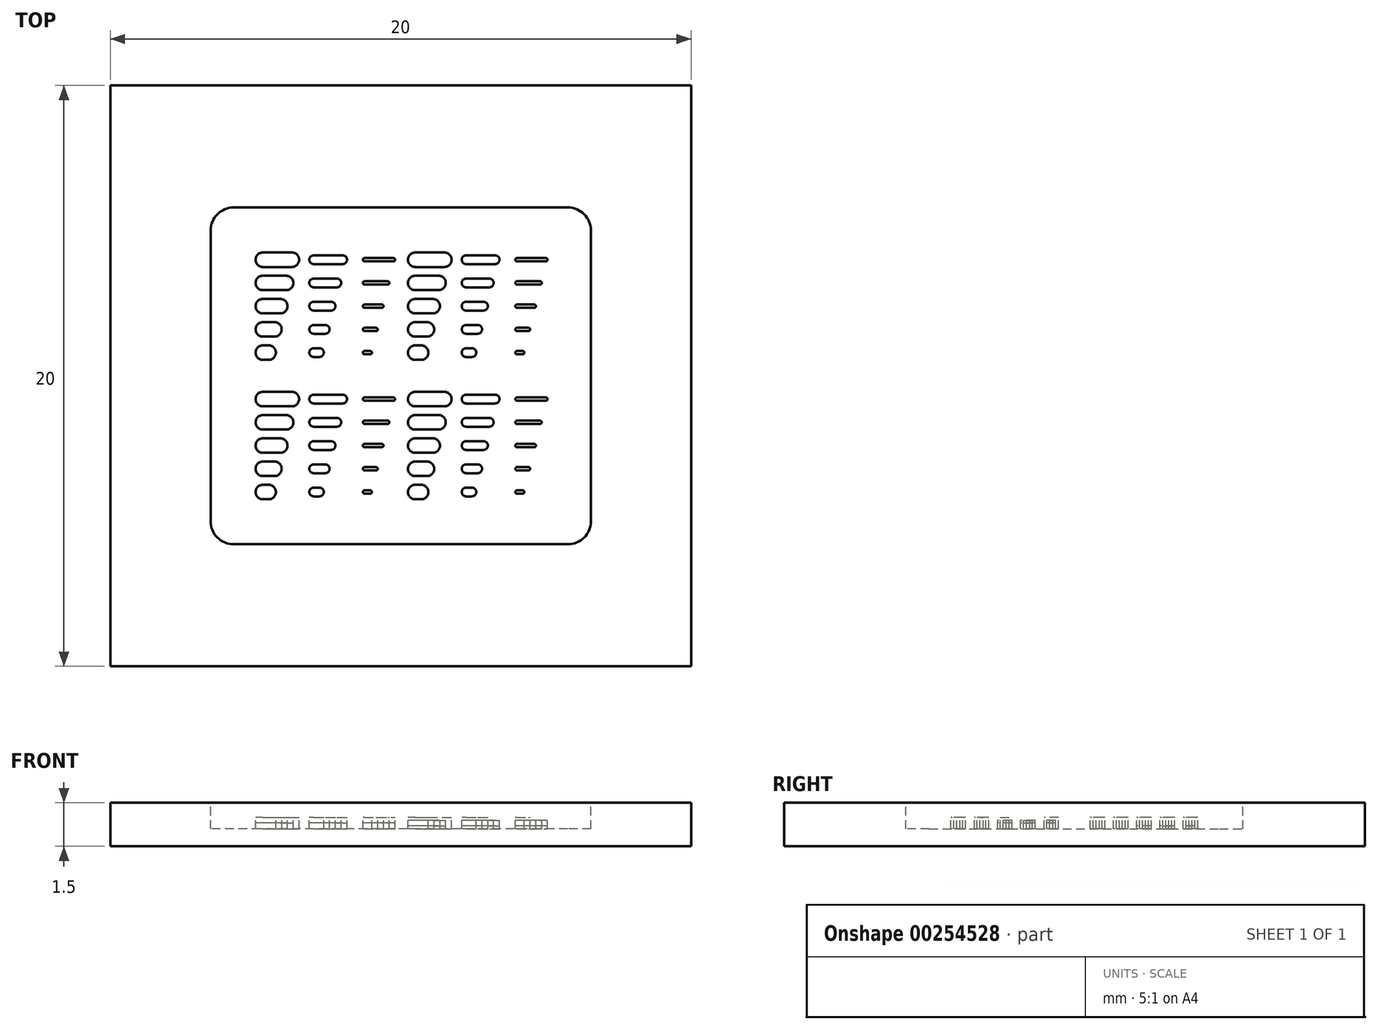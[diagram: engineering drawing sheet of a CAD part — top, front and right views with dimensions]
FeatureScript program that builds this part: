
annotation { "Feature Type Name" : "Feature", "Feature Type Description" : "" }
export const myFeature = defineFeature(function(context is Context, id is Id, definition is map)
    precondition{}
    {
        {
            var Q0;
            Q0=qCreatedBy(makeId("Top.planeOp"),FACE);
            var sketch = newSketch(context, id + "F0", { "sketchPlane" : qUnion([Q0])});
            skLineSegment(sketch, "E0.bottom", {"start": v(10, 10) * mm, "end": v(-10, 10) * mm});
            skLineSegment(sketch, "E0.top", {"start": v(10, -10) * mm, "end": v(-10, -10) * mm});
            skLineSegment(sketch, "E0.left", {"start": v(10, 10) * mm, "end": v(10, -10) * mm});
            skLineSegment(sketch, "E0.right", {"start": v(-10, 10) * mm, "end": v(-10, -10) * mm});
            skPoint(sketch, "E0.middle", {"position": v(0, 0) * mm});
            skSolve(sketch);
        }
        {
            var Q0;
            Q0=qSketchRegion(id+"F0",true);
            extrude(context, id + "F1", {"entities" : qUnion([Q0]), "oppositeDirection" : true, "depth" : 1 * mm});
        }
        {
            var Q0;
            Q0=makeQuery(id+"F1.opExtrude","CAP_FACE",FACE,{"disambiguationData":[OSD([sQuery(id+"F0.wireOp",EDGE,"E0.bottom"),sQuery(id+"F0.wireOp",EDGE,"E0.top"),sQuery(id+"F0.wireOp",EDGE,"E0.left"),sQuery(id+"F0.wireOp",EDGE,"E0.right")])],"isStart":true});
            var sketch = newSketch(context, id + "F2", { "sketchPlane" : qUnion([Q0])});
            skLineSegment(sketch, "E1.bottom", {"start": v(5.75, -5) * mm, "end": v(-5.75, -5) * mm});
            skLineSegment(sketch, "E1.top", {"start": v(5.75, 5) * mm, "end": v(-5.75, 5) * mm});
            skLineSegment(sketch, "E1.left", {"start": v(5.75, -5) * mm, "end": v(5.75, 5) * mm});
            skLineSegment(sketch, "E1.right", {"start": v(-5.75, -5) * mm, "end": v(-5.75, 5) * mm});
            skLineSegment(sketch, "E2", {"start": v(-4.75, 4) * mm, "end": v(-3.75, 4) * mm, "construction": true});
            skLineSegment(sketch, "E3", {"start": v(-4.75, 3.2) * mm, "end": v(-3.95, 3.2) * mm, "construction": true});
            skLineSegment(sketch, "E4", {"start": v(-4.75, 2.4) * mm, "end": v(-4.15, 2.4) * mm, "construction": true});
            skLineSegment(sketch, "E5", {"start": v(-4.75, 1.6) * mm, "end": v(-4.35, 1.6) * mm, "construction": true});
            skLineSegment(sketch, "E6", {"start": v(-4.75, 0.8) * mm, "end": v(-4.55, 0.8) * mm, "construction": true});
            skLineSegment(sketch, "E7.1.0.0", {"start": v(-3, 3.2) * mm, "end": v(-2.2, 3.2) * mm, "construction": true});
            skLineSegment(sketch, "E7.1.0.1", {"start": v(-3, 4) * mm, "end": v(-2, 4) * mm, "construction": true});
            skLineSegment(sketch, "E7.1.0.2", {"start": v(-3, 2.4) * mm, "end": v(-2.4, 2.4) * mm, "construction": true});
            skLineSegment(sketch, "E7.1.0.3", {"start": v(-3, 1.6) * mm, "end": v(-2.6, 1.6) * mm, "construction": true});
            skLineSegment(sketch, "E7.1.0.4", {"start": v(-3, 0.8) * mm, "end": v(-2.8, 0.8) * mm, "construction": true});
            skLineSegment(sketch, "E7.2.0.0", {"start": v(-1.25, 3.2) * mm, "end": v(-0.45, 3.2) * mm, "construction": true});
            skLineSegment(sketch, "E7.2.0.1", {"start": v(-1.25, 4) * mm, "end": v(-0.25, 4) * mm, "construction": true});
            skLineSegment(sketch, "E7.2.0.2", {"start": v(-1.25, 2.4) * mm, "end": v(-0.65, 2.4) * mm, "construction": true});
            skLineSegment(sketch, "E7.2.0.3", {"start": v(-1.25, 1.6) * mm, "end": v(-0.85, 1.6) * mm, "construction": true});
            skLineSegment(sketch, "E7.2.0.4", {"start": v(-1.25, 0.8) * mm, "end": v(-1.05, 0.8) * mm, "construction": true});
            skLineSegment(sketch, "E7.direction1", {"start": v(-4.75, 0.8) * mm, "end": v(-3, 0.8) * mm, "construction": true});
            skLineSegment(sketch, "E7.direction2", {"start": v(-4.75, 0.8) * mm, "end": v(-4.75, -4) * mm, "construction": true});
            skLineSegment(sketch, "E8.0", {"start": v(5.75, 5.8) * mm, "end": v(-5.75, 5.8) * mm});
            skLineSegment(sketch, "E8.1", {"start": v(6.55, -5) * mm, "end": v(6.55, 5) * mm});
            skLineSegment(sketch, "E8.2", {"start": v(5.75, -5.8) * mm, "end": v(-5.75, -5.8) * mm});
            skLineSegment(sketch, "E8.3", {"start": v(-6.55, -5) * mm, "end": v(-6.55, 5) * mm});
            skPoint(sketch, "E9.visualSharp", {"position": v(-6.55, 5.8) * mm});
            skArc(sketch, "E9.filletArc", {"start": v(-5.75, 5.8) * mm, "mid": v(-6.32, 5.57) * mm, "end": v(-6.55, 5) * mm});
            skPoint(sketch, "E10.visualSharp", {"position": v(6.55, 5.8) * mm});
            skArc(sketch, "E10.filletArc", {"start": v(6.55, 5) * mm, "mid": v(6.32, 5.57) * mm, "end": v(5.75, 5.8) * mm});
            skPoint(sketch, "E11.visualSharp", {"position": v(6.55, -5.8) * mm});
            skArc(sketch, "E11.filletArc", {"start": v(5.75, -5.8) * mm, "mid": v(6.32, -5.57) * mm, "end": v(6.55, -5) * mm});
            skPoint(sketch, "E12.visualSharp", {"position": v(-6.55, -5.8) * mm});
            skArc(sketch, "E12.filletArc", {"start": v(-6.55, -5) * mm, "mid": v(-6.32, -5.57) * mm, "end": v(-5.75, -5.8) * mm});
            skArc(sketch, "E13.0.startCap", {"start": v(-4.75, 0.55) * mm, "mid": v(-5, 0.8) * mm, "end": v(-4.75, 1.05) * mm});
            skArc(sketch, "E13.0.endCap", {"start": v(-4.55, 1.05) * mm, "mid": v(-4.3, 0.8) * mm, "end": v(-4.55, 0.55) * mm});
            skLineSegment(sketch, "E13.0.left", {"start": v(-4.75, 1.05) * mm, "end": v(-4.55, 1.05) * mm});
            skLineSegment(sketch, "E13.0.right", {"start": v(-4.75, 0.55) * mm, "end": v(-4.55, 0.55) * mm});
            skArc(sketch, "E13.1.startCap", {"start": v(-4.75, 1.35) * mm, "mid": v(-5, 1.6) * mm, "end": v(-4.75, 1.85) * mm});
            skArc(sketch, "E13.1.endCap", {"start": v(-4.35, 1.85) * mm, "mid": v(-4.1, 1.6) * mm, "end": v(-4.35, 1.35) * mm});
            skLineSegment(sketch, "E13.1.left", {"start": v(-4.75, 1.85) * mm, "end": v(-4.35, 1.85) * mm});
            skLineSegment(sketch, "E13.1.right", {"start": v(-4.75, 1.35) * mm, "end": v(-4.35, 1.35) * mm});
            skArc(sketch, "E13.2.startCap", {"start": v(-4.75, 2.15) * mm, "mid": v(-5, 2.4) * mm, "end": v(-4.75, 2.65) * mm});
            skArc(sketch, "E13.2.endCap", {"start": v(-4.15, 2.65) * mm, "mid": v(-3.9, 2.4) * mm, "end": v(-4.15, 2.15) * mm});
            skLineSegment(sketch, "E13.2.left", {"start": v(-4.75, 2.65) * mm, "end": v(-4.15, 2.65) * mm});
            skLineSegment(sketch, "E13.2.right", {"start": v(-4.75, 2.15) * mm, "end": v(-4.15, 2.15) * mm});
            skArc(sketch, "E13.3.startCap", {"start": v(-4.75, 2.95) * mm, "mid": v(-5, 3.2) * mm, "end": v(-4.75, 3.45) * mm});
            skArc(sketch, "E13.3.endCap", {"start": v(-3.95, 3.45) * mm, "mid": v(-3.7, 3.2) * mm, "end": v(-3.95, 2.95) * mm});
            skLineSegment(sketch, "E13.3.left", {"start": v(-4.75, 3.45) * mm, "end": v(-3.95, 3.45) * mm});
            skLineSegment(sketch, "E13.3.right", {"start": v(-4.75, 2.95) * mm, "end": v(-3.95, 2.95) * mm});
            skArc(sketch, "E13.4.startCap", {"start": v(-4.75, 3.75) * mm, "mid": v(-5, 4) * mm, "end": v(-4.75, 4.25) * mm});
            skArc(sketch, "E13.4.endCap", {"start": v(-3.75, 4.25) * mm, "mid": v(-3.5, 4) * mm, "end": v(-3.75, 3.75) * mm});
            skLineSegment(sketch, "E13.4.left", {"start": v(-4.75, 4.25) * mm, "end": v(-3.75, 4.25) * mm});
            skLineSegment(sketch, "E13.4.right", {"start": v(-4.75, 3.75) * mm, "end": v(-3.75, 3.75) * mm});
            skArc(sketch, "E14.0.startCap", {"start": v(-3, 0.65) * mm, "mid": v(-3.15, 0.8) * mm, "end": v(-3, 0.95) * mm});
            skArc(sketch, "E14.0.endCap", {"start": v(-2.8, 0.95) * mm, "mid": v(-2.65, 0.8) * mm, "end": v(-2.8, 0.65) * mm});
            skLineSegment(sketch, "E14.0.left", {"start": v(-3, 0.95) * mm, "end": v(-2.8, 0.95) * mm});
            skLineSegment(sketch, "E14.0.right", {"start": v(-3, 0.65) * mm, "end": v(-2.8, 0.65) * mm});
            skArc(sketch, "E14.1.startCap", {"start": v(-3, 1.45) * mm, "mid": v(-3.15, 1.6) * mm, "end": v(-3, 1.75) * mm});
            skArc(sketch, "E14.1.endCap", {"start": v(-2.6, 1.75) * mm, "mid": v(-2.45, 1.6) * mm, "end": v(-2.6, 1.45) * mm});
            skLineSegment(sketch, "E14.1.left", {"start": v(-3, 1.75) * mm, "end": v(-2.6, 1.75) * mm});
            skLineSegment(sketch, "E14.1.right", {"start": v(-3, 1.45) * mm, "end": v(-2.6, 1.45) * mm});
            skArc(sketch, "E14.2.startCap", {"start": v(-3, 2.25) * mm, "mid": v(-3.15, 2.4) * mm, "end": v(-3, 2.55) * mm});
            skArc(sketch, "E14.2.endCap", {"start": v(-2.4, 2.55) * mm, "mid": v(-2.25, 2.4) * mm, "end": v(-2.4, 2.25) * mm});
            skLineSegment(sketch, "E14.2.left", {"start": v(-3, 2.55) * mm, "end": v(-2.4, 2.55) * mm});
            skLineSegment(sketch, "E14.2.right", {"start": v(-3, 2.25) * mm, "end": v(-2.4, 2.25) * mm});
            skArc(sketch, "E14.3.startCap", {"start": v(-3, 3.05) * mm, "mid": v(-3.15, 3.2) * mm, "end": v(-3, 3.35) * mm});
            skArc(sketch, "E14.3.endCap", {"start": v(-2.2, 3.35) * mm, "mid": v(-2.05, 3.2) * mm, "end": v(-2.2, 3.05) * mm});
            skLineSegment(sketch, "E14.3.left", {"start": v(-3, 3.35) * mm, "end": v(-2.2, 3.35) * mm});
            skLineSegment(sketch, "E14.3.right", {"start": v(-3, 3.05) * mm, "end": v(-2.2, 3.05) * mm});
            skArc(sketch, "E14.4.startCap", {"start": v(-3, 3.85) * mm, "mid": v(-3.15, 4) * mm, "end": v(-3, 4.15) * mm});
            skArc(sketch, "E14.4.endCap", {"start": v(-2, 4.15) * mm, "mid": v(-1.85, 4) * mm, "end": v(-2, 3.85) * mm});
            skLineSegment(sketch, "E14.4.left", {"start": v(-3, 4.15) * mm, "end": v(-2, 4.15) * mm});
            skLineSegment(sketch, "E14.4.right", {"start": v(-3, 3.85) * mm, "end": v(-2, 3.85) * mm});
            skArc(sketch, "E15.0.startCap", {"start": v(-1.25, 0.74) * mm, "mid": v(-1.3, 0.8) * mm, "end": v(-1.25, 0.85) * mm});
            skArc(sketch, "E15.0.endCap", {"start": v(-1.05, 0.85) * mm, "mid": v(-1, 0.8) * mm, "end": v(-1.05, 0.75) * mm});
            skLineSegment(sketch, "E15.0.left", {"start": v(-1.25, 0.85) * mm, "end": v(-1.05, 0.85) * mm});
            skLineSegment(sketch, "E15.0.right", {"start": v(-1.25, 0.74) * mm, "end": v(-1.05, 0.74) * mm});
            skArc(sketch, "E15.1.startCap", {"start": v(-1.25, 1.54) * mm, "mid": v(-1.3, 1.6) * mm, "end": v(-1.25, 1.65) * mm});
            skArc(sketch, "E15.1.endCap", {"start": v(-0.85, 1.65) * mm, "mid": v(-0.8, 1.6) * mm, "end": v(-0.85, 1.54) * mm});
            skLineSegment(sketch, "E15.1.left", {"start": v(-1.25, 1.65) * mm, "end": v(-0.85, 1.65) * mm});
            skLineSegment(sketch, "E15.1.right", {"start": v(-1.25, 1.54) * mm, "end": v(-0.85, 1.54) * mm});
            skArc(sketch, "E15.2.startCap", {"start": v(-1.25, 2.34) * mm, "mid": v(-1.3, 2.4) * mm, "end": v(-1.25, 2.45) * mm});
            skArc(sketch, "E15.2.endCap", {"start": v(-0.65, 2.45) * mm, "mid": v(-0.6, 2.4) * mm, "end": v(-0.65, 2.34) * mm});
            skLineSegment(sketch, "E15.2.left", {"start": v(-1.25, 2.45) * mm, "end": v(-0.65, 2.45) * mm});
            skLineSegment(sketch, "E15.2.right", {"start": v(-1.25, 2.34) * mm, "end": v(-0.65, 2.34) * mm});
            skArc(sketch, "E15.3.startCap", {"start": v(-1.25, 3.14) * mm, "mid": v(-1.3, 3.2) * mm, "end": v(-1.25, 3.25) * mm});
            skArc(sketch, "E15.3.endCap", {"start": v(-0.45, 3.25) * mm, "mid": v(-0.4, 3.2) * mm, "end": v(-0.45, 3.14) * mm});
            skLineSegment(sketch, "E15.3.left", {"start": v(-1.25, 3.25) * mm, "end": v(-0.45, 3.25) * mm});
            skLineSegment(sketch, "E15.3.right", {"start": v(-1.25, 3.14) * mm, "end": v(-0.45, 3.14) * mm});
            skArc(sketch, "E15.4.startCap", {"start": v(-1.25, 3.94) * mm, "mid": v(-1.3, 4) * mm, "end": v(-1.25, 4.05) * mm});
            skArc(sketch, "E15.4.endCap", {"start": v(-0.25, 4.05) * mm, "mid": v(-0.2, 4) * mm, "end": v(-0.25, 3.94) * mm});
            skLineSegment(sketch, "E15.4.left", {"start": v(-1.25, 4.05) * mm, "end": v(-0.25, 4.05) * mm});
            skLineSegment(sketch, "E15.4.right", {"start": v(-1.25, 3.94) * mm, "end": v(-0.25, 3.94) * mm});
            skLineSegment(sketch, "E16.0.1.0", {"start": v(-1.25, -1.54) * mm, "end": v(-0.45, -1.54) * mm});
            skArc(sketch, "E16.0.1.1", {"start": v(-4.35, -2.95) * mm, "mid": v(-4.1, -3.2) * mm, "end": v(-4.35, -3.45) * mm});
            skLineSegment(sketch, "E16.0.1.2", {"start": v(-4.75, -2.65) * mm, "end": v(-4.15, -2.65) * mm});
            skArc(sketch, "E16.0.1.3", {"start": v(-4.75, -1.05) * mm, "mid": v(-5, -0.8) * mm, "end": v(-4.75, -0.55) * mm});
            skArc(sketch, "E16.0.1.4", {"start": v(-1.05, -3.95) * mm, "mid": v(-1, -4) * mm, "end": v(-1.05, -4.06) * mm});
            skArc(sketch, "E16.0.1.5", {"start": v(-0.45, -1.55) * mm, "mid": v(-0.4, -1.6) * mm, "end": v(-0.45, -1.66) * mm});
            skArc(sketch, "E16.0.1.6", {"start": v(-2.6, -3.05) * mm, "mid": v(-2.45, -3.2) * mm, "end": v(-2.6, -3.35) * mm});
            skLineSegment(sketch, "E16.0.1.7", {"start": v(-1.25, -1.65) * mm, "end": v(-0.45, -1.65) * mm});
            skLineSegment(sketch, "E16.0.1.8", {"start": v(-4.75, -1.6) * mm, "end": v(-3.95, -1.6) * mm, "construction": true});
            skLineSegment(sketch, "E16.0.1.9", {"start": v(-4.75, -1.85) * mm, "end": v(-3.95, -1.85) * mm});
            skArc(sketch, "E16.0.1.10", {"start": v(-4.15, -2.15) * mm, "mid": v(-3.9, -2.4) * mm, "end": v(-4.15, -2.65) * mm});
            skArc(sketch, "E16.0.1.11", {"start": v(-3, -4.15) * mm, "mid": v(-3.15, -4) * mm, "end": v(-3, -3.85) * mm});
            skLineSegment(sketch, "E16.0.1.12", {"start": v(-1.25, -0.74) * mm, "end": v(-0.25, -0.74) * mm});
            skArc(sketch, "E16.0.1.13", {"start": v(-2.4, -2.25) * mm, "mid": v(-2.25, -2.4) * mm, "end": v(-2.4, -2.55) * mm});
            skArc(sketch, "E16.0.1.14", {"start": v(-4.75, -4.25) * mm, "mid": v(-5, -4) * mm, "end": v(-4.75, -3.75) * mm});
            skLineSegment(sketch, "E16.0.1.15", {"start": v(-1.25, -0.85) * mm, "end": v(-0.25, -0.85) * mm});
            skLineSegment(sketch, "E16.0.1.16", {"start": v(-4.75, -0.8) * mm, "end": v(-3.75, -0.8) * mm, "construction": true});
            skLineSegment(sketch, "E16.0.1.17", {"start": v(-1.25, -2.45) * mm, "end": v(-0.65, -2.45) * mm});
            skLineSegment(sketch, "E16.0.1.18", {"start": v(-3, -0.95) * mm, "end": v(-2, -0.95) * mm});
            skArc(sketch, "E16.0.1.19", {"start": v(-0.65, -2.35) * mm, "mid": v(-0.6, -2.4) * mm, "end": v(-0.65, -2.46) * mm});
            skLineSegment(sketch, "E16.0.1.20", {"start": v(-4.75, -1.05) * mm, "end": v(-3.75, -1.05) * mm});
            skArc(sketch, "E16.0.1.21", {"start": v(-2, -0.65) * mm, "mid": v(-1.85, -0.8) * mm, "end": v(-2, -0.95) * mm});
            skLineSegment(sketch, "E16.0.1.22", {"start": v(-3, -2.55) * mm, "end": v(-2.4, -2.55) * mm});
            skLineSegment(sketch, "E16.0.1.23", {"start": v(-1.25, -2.4) * mm, "end": v(-0.65, -2.4) * mm, "construction": true});
            skLineSegment(sketch, "E16.0.1.24", {"start": v(-4.75, -2.4) * mm, "end": v(-4.15, -2.4) * mm, "construction": true});
            skArc(sketch, "E16.0.1.25", {"start": v(-3, -2.55) * mm, "mid": v(-3.15, -2.4) * mm, "end": v(-3, -2.25) * mm});
            skLineSegment(sketch, "E16.0.1.26", {"start": v(-1.25, -0.8) * mm, "end": v(-0.25, -0.8) * mm, "construction": true});
            skLineSegment(sketch, "E16.0.1.27", {"start": v(-3, -0.8) * mm, "end": v(-2, -0.8) * mm, "construction": true});
            skArc(sketch, "E16.0.1.28", {"start": v(-0.25, -0.75) * mm, "mid": v(-0.2, -0.8) * mm, "end": v(-0.25, -0.86) * mm});
            skArc(sketch, "E16.0.1.29", {"start": v(-3.95, -1.35) * mm, "mid": v(-3.7, -1.6) * mm, "end": v(-3.95, -1.85) * mm});
            skLineSegment(sketch, "E16.0.1.30", {"start": v(-4.75, -4) * mm, "end": v(-3, -4) * mm, "construction": true});
            skLineSegment(sketch, "E16.0.1.31", {"start": v(-3, -1.75) * mm, "end": v(-2.2, -1.75) * mm});
            skArc(sketch, "E16.0.1.32", {"start": v(-4.75, -1.85) * mm, "mid": v(-5, -1.6) * mm, "end": v(-4.75, -1.35) * mm});
            skLineSegment(sketch, "E16.0.1.33", {"start": v(-1.25, -1.6) * mm, "end": v(-0.45, -1.6) * mm, "construction": true});
            skLineSegment(sketch, "E16.0.1.34", {"start": v(-3, -2.4) * mm, "end": v(-2.4, -2.4) * mm, "construction": true});
            skLineSegment(sketch, "E16.0.1.35", {"start": v(-4.75, -1.35) * mm, "end": v(-3.95, -1.35) * mm});
            skLineSegment(sketch, "E16.0.1.36", {"start": v(-3, -1.45) * mm, "end": v(-2.2, -1.45) * mm});
            skLineSegment(sketch, "E16.0.1.37", {"start": v(-3, -0.65) * mm, "end": v(-2, -0.65) * mm});
            skArc(sketch, "E16.0.1.38", {"start": v(-3, -0.95) * mm, "mid": v(-3.15, -0.8) * mm, "end": v(-3, -0.65) * mm});
            skArc(sketch, "E16.0.1.39", {"start": v(-4.75, -3.45) * mm, "mid": v(-5, -3.2) * mm, "end": v(-4.75, -2.95) * mm});
            skArc(sketch, "E16.0.1.40", {"start": v(-3.75, -0.55) * mm, "mid": v(-3.5, -0.8) * mm, "end": v(-3.75, -1.05) * mm});
            skArc(sketch, "E16.0.1.41", {"start": v(-3, -3.35) * mm, "mid": v(-3.15, -3.2) * mm, "end": v(-3, -3.05) * mm});
            skLineSegment(sketch, "E16.0.1.42", {"start": v(-4.75, -2.15) * mm, "end": v(-4.15, -2.15) * mm});
            skArc(sketch, "E16.0.1.43", {"start": v(-4.55, -3.75) * mm, "mid": v(-4.3, -4) * mm, "end": v(-4.55, -4.25) * mm});
            skLineSegment(sketch, "E16.0.1.44", {"start": v(-1.25, -2.34) * mm, "end": v(-0.65, -2.34) * mm});
            skLineSegment(sketch, "E16.0.1.45", {"start": v(-3, -1.6) * mm, "end": v(-2.2, -1.6) * mm, "construction": true});
            skArc(sketch, "E16.0.1.46", {"start": v(-4.75, -2.65) * mm, "mid": v(-5, -2.4) * mm, "end": v(-4.75, -2.15) * mm});
            skLineSegment(sketch, "E16.0.1.47", {"start": v(-4.75, -0.55) * mm, "end": v(-3.75, -0.55) * mm});
            skArc(sketch, "E16.0.1.48", {"start": v(-0.85, -3.15) * mm, "mid": v(-0.8, -3.2) * mm, "end": v(-0.85, -3.26) * mm});
            skArc(sketch, "E16.0.1.49", {"start": v(-2.8, -3.85) * mm, "mid": v(-2.65, -4) * mm, "end": v(-2.8, -4.15) * mm});
            skLineSegment(sketch, "E16.0.1.50", {"start": v(-3, -2.25) * mm, "end": v(-2.4, -2.25) * mm});
            skArc(sketch, "E16.0.1.51", {"start": v(-2.2, -1.45) * mm, "mid": v(-2.05, -1.6) * mm, "end": v(-2.2, -1.75) * mm});
            skLineSegment(sketch, "E16.0.1.52", {"start": v(-4.75, -4.25) * mm, "end": v(-4.55, -4.25) * mm});
            skArc(sketch, "E16.0.1.53", {"start": v(-1.25, -4.06) * mm, "mid": v(-1.3, -4) * mm, "end": v(-1.25, -3.94) * mm});
            skLineSegment(sketch, "E16.0.1.54", {"start": v(-1.25, -4.05) * mm, "end": v(-1.05, -4.05) * mm});
            skLineSegment(sketch, "E16.0.1.55", {"start": v(-3, -3.35) * mm, "end": v(-2.6, -3.35) * mm});
            skLineSegment(sketch, "E16.0.1.56", {"start": v(-1.25, -3.14) * mm, "end": v(-0.85, -3.14) * mm});
            skLineSegment(sketch, "E16.0.1.57", {"start": v(-3, -4) * mm, "end": v(-2.8, -4) * mm, "construction": true});
            skLineSegment(sketch, "E16.0.1.58", {"start": v(-4.75, -2.95) * mm, "end": v(-4.35, -2.95) * mm});
            skLineSegment(sketch, "E16.0.1.59", {"start": v(-4.75, -4) * mm, "end": v(-4.75, -8.8) * mm, "construction": true});
            skLineSegment(sketch, "E16.0.1.60", {"start": v(-1.25, -3.25) * mm, "end": v(-0.85, -3.25) * mm});
            skLineSegment(sketch, "E16.0.1.61", {"start": v(-3, -3.85) * mm, "end": v(-2.8, -3.85) * mm});
            skLineSegment(sketch, "E16.0.1.62", {"start": v(-1.25, -3.94) * mm, "end": v(-1.05, -3.94) * mm});
            skLineSegment(sketch, "E16.0.1.63", {"start": v(-3, -4.15) * mm, "end": v(-2.8, -4.15) * mm});
            skLineSegment(sketch, "E16.0.1.64", {"start": v(-4.75, -3.2) * mm, "end": v(-4.35, -3.2) * mm, "construction": true});
            skLineSegment(sketch, "E16.0.1.65", {"start": v(-3, -3.05) * mm, "end": v(-2.6, -3.05) * mm});
            skLineSegment(sketch, "E16.0.1.66", {"start": v(-1.25, -3.2) * mm, "end": v(-0.85, -3.2) * mm, "construction": true});
            skLineSegment(sketch, "E16.0.1.67", {"start": v(-1.25, -4) * mm, "end": v(-1.05, -4) * mm, "construction": true});
            skLineSegment(sketch, "E16.0.1.68", {"start": v(-4.75, -3.75) * mm, "end": v(-4.55, -3.75) * mm});
            skArc(sketch, "E16.0.1.69", {"start": v(-3, -1.75) * mm, "mid": v(-3.15, -1.6) * mm, "end": v(-3, -1.45) * mm});
            skArc(sketch, "E16.0.1.70", {"start": v(-1.25, -3.26) * mm, "mid": v(-1.3, -3.2) * mm, "end": v(-1.25, -3.15) * mm});
            skLineSegment(sketch, "E16.0.1.71", {"start": v(-4.75, -3.45) * mm, "end": v(-4.35, -3.45) * mm});
            skArc(sketch, "E16.0.1.72", {"start": v(-1.25, -1.66) * mm, "mid": v(-1.3, -1.6) * mm, "end": v(-1.25, -1.55) * mm});
            skArc(sketch, "E16.0.1.73", {"start": v(-1.25, -2.46) * mm, "mid": v(-1.3, -2.4) * mm, "end": v(-1.25, -2.35) * mm});
            skLineSegment(sketch, "E16.0.1.74", {"start": v(-3, -3.2) * mm, "end": v(-2.6, -3.2) * mm, "construction": true});
            skArc(sketch, "E16.0.1.75", {"start": v(-1.25, -0.86) * mm, "mid": v(-1.3, -0.8) * mm, "end": v(-1.25, -0.75) * mm});
            skLineSegment(sketch, "E16.0.1.76", {"start": v(-4.75, -4) * mm, "end": v(-4.55, -4) * mm, "construction": true});
            skLineSegment(sketch, "E16.1.0.0", {"start": v(4, 3.25) * mm, "end": v(4.8, 3.25) * mm});
            skArc(sketch, "E16.1.0.1", {"start": v(0.9, 1.85) * mm, "mid": v(1.15, 1.6) * mm, "end": v(0.9, 1.35) * mm});
            skLineSegment(sketch, "E16.1.0.2", {"start": v(0.5, 2.15) * mm, "end": v(1.1, 2.15) * mm});
            skArc(sketch, "E16.1.0.3", {"start": v(0.5, 3.75) * mm, "mid": v(0.25, 4) * mm, "end": v(0.5, 4.25) * mm});
            skArc(sketch, "E16.1.0.4", {"start": v(4.2, 0.85) * mm, "mid": v(4.25, 0.8) * mm, "end": v(4.2, 0.74) * mm});
            skArc(sketch, "E16.1.0.5", {"start": v(4.8, 3.25) * mm, "mid": v(4.85, 3.2) * mm, "end": v(4.8, 3.14) * mm});
            skArc(sketch, "E16.1.0.6", {"start": v(2.65, 1.75) * mm, "mid": v(2.8, 1.6) * mm, "end": v(2.65, 1.45) * mm});
            skLineSegment(sketch, "E16.1.0.7", {"start": v(4, 3.14) * mm, "end": v(4.8, 3.14) * mm});
            skLineSegment(sketch, "E16.1.0.8", {"start": v(0.5, 3.2) * mm, "end": v(1.3, 3.2) * mm, "construction": true});
            skLineSegment(sketch, "E16.1.0.9", {"start": v(0.5, 2.95) * mm, "end": v(1.3, 2.95) * mm});
            skArc(sketch, "E16.1.0.10", {"start": v(1.1, 2.65) * mm, "mid": v(1.35, 2.4) * mm, "end": v(1.1, 2.15) * mm});
            skArc(sketch, "E16.1.0.11", {"start": v(2.25, 0.65) * mm, "mid": v(2.1, 0.8) * mm, "end": v(2.25, 0.95) * mm});
            skLineSegment(sketch, "E16.1.0.12", {"start": v(4, 4.05) * mm, "end": v(5, 4.05) * mm});
            skArc(sketch, "E16.1.0.13", {"start": v(2.85, 2.55) * mm, "mid": v(3, 2.4) * mm, "end": v(2.85, 2.25) * mm});
            skArc(sketch, "E16.1.0.14", {"start": v(0.5, 0.55) * mm, "mid": v(0.25, 0.8) * mm, "end": v(0.5, 1.05) * mm});
            skLineSegment(sketch, "E16.1.0.15", {"start": v(4, 3.94) * mm, "end": v(5, 3.94) * mm});
            skLineSegment(sketch, "E16.1.0.16", {"start": v(0.5, 4) * mm, "end": v(1.5, 4) * mm, "construction": true});
            skLineSegment(sketch, "E16.1.0.17", {"start": v(4, 2.34) * mm, "end": v(4.6, 2.34) * mm});
            skLineSegment(sketch, "E16.1.0.18", {"start": v(2.25, 3.85) * mm, "end": v(3.25, 3.85) * mm});
            skArc(sketch, "E16.1.0.19", {"start": v(4.6, 2.45) * mm, "mid": v(4.65, 2.4) * mm, "end": v(4.6, 2.34) * mm});
            skLineSegment(sketch, "E16.1.0.20", {"start": v(0.5, 3.75) * mm, "end": v(1.5, 3.75) * mm});
            skArc(sketch, "E16.1.0.21", {"start": v(3.25, 4.15) * mm, "mid": v(3.4, 4) * mm, "end": v(3.25, 3.85) * mm});
            skLineSegment(sketch, "E16.1.0.22", {"start": v(2.25, 2.25) * mm, "end": v(2.85, 2.25) * mm});
            skLineSegment(sketch, "E16.1.0.23", {"start": v(4, 2.4) * mm, "end": v(4.6, 2.4) * mm, "construction": true});
            skLineSegment(sketch, "E16.1.0.24", {"start": v(0.5, 2.4) * mm, "end": v(1.1, 2.4) * mm, "construction": true});
            skArc(sketch, "E16.1.0.25", {"start": v(2.25, 2.25) * mm, "mid": v(2.1, 2.4) * mm, "end": v(2.25, 2.55) * mm});
            skLineSegment(sketch, "E16.1.0.26", {"start": v(4, 4) * mm, "end": v(5, 4) * mm, "construction": true});
            skLineSegment(sketch, "E16.1.0.27", {"start": v(2.25, 4) * mm, "end": v(3.25, 4) * mm, "construction": true});
            skArc(sketch, "E16.1.0.28", {"start": v(5, 4.05) * mm, "mid": v(5.05, 4) * mm, "end": v(5, 3.94) * mm});
            skArc(sketch, "E16.1.0.29", {"start": v(1.3, 3.45) * mm, "mid": v(1.55, 3.2) * mm, "end": v(1.3, 2.95) * mm});
            skLineSegment(sketch, "E16.1.0.30", {"start": v(0.5, 0.8) * mm, "end": v(2.25, 0.8) * mm, "construction": true});
            skLineSegment(sketch, "E16.1.0.31", {"start": v(2.25, 3.05) * mm, "end": v(3.05, 3.05) * mm});
            skArc(sketch, "E16.1.0.32", {"start": v(0.5, 2.95) * mm, "mid": v(0.25, 3.2) * mm, "end": v(0.5, 3.45) * mm});
            skLineSegment(sketch, "E16.1.0.33", {"start": v(4, 3.2) * mm, "end": v(4.8, 3.2) * mm, "construction": true});
            skLineSegment(sketch, "E16.1.0.34", {"start": v(2.25, 2.4) * mm, "end": v(2.85, 2.4) * mm, "construction": true});
            skLineSegment(sketch, "E16.1.0.35", {"start": v(0.5, 3.45) * mm, "end": v(1.3, 3.45) * mm});
            skLineSegment(sketch, "E16.1.0.36", {"start": v(2.25, 3.35) * mm, "end": v(3.05, 3.35) * mm});
            skLineSegment(sketch, "E16.1.0.37", {"start": v(2.25, 4.15) * mm, "end": v(3.25, 4.15) * mm});
            skArc(sketch, "E16.1.0.38", {"start": v(2.25, 3.85) * mm, "mid": v(2.1, 4) * mm, "end": v(2.25, 4.15) * mm});
            skArc(sketch, "E16.1.0.39", {"start": v(0.5, 1.35) * mm, "mid": v(0.25, 1.6) * mm, "end": v(0.5, 1.85) * mm});
            skArc(sketch, "E16.1.0.40", {"start": v(1.5, 4.25) * mm, "mid": v(1.75, 4) * mm, "end": v(1.5, 3.75) * mm});
            skArc(sketch, "E16.1.0.41", {"start": v(2.25, 1.45) * mm, "mid": v(2.1, 1.6) * mm, "end": v(2.25, 1.75) * mm});
            skLineSegment(sketch, "E16.1.0.42", {"start": v(0.5, 2.65) * mm, "end": v(1.1, 2.65) * mm});
            skArc(sketch, "E16.1.0.43", {"start": v(0.7, 1.05) * mm, "mid": v(0.95, 0.8) * mm, "end": v(0.7, 0.55) * mm});
            skLineSegment(sketch, "E16.1.0.44", {"start": v(4, 2.45) * mm, "end": v(4.6, 2.45) * mm});
            skLineSegment(sketch, "E16.1.0.45", {"start": v(2.25, 3.2) * mm, "end": v(3.05, 3.2) * mm, "construction": true});
            skArc(sketch, "E16.1.0.46", {"start": v(0.5, 2.15) * mm, "mid": v(0.25, 2.4) * mm, "end": v(0.5, 2.65) * mm});
            skLineSegment(sketch, "E16.1.0.47", {"start": v(0.5, 4.25) * mm, "end": v(1.5, 4.25) * mm});
            skArc(sketch, "E16.1.0.48", {"start": v(4.4, 1.65) * mm, "mid": v(4.45, 1.6) * mm, "end": v(4.4, 1.54) * mm});
            skArc(sketch, "E16.1.0.49", {"start": v(2.45, 0.95) * mm, "mid": v(2.6, 0.8) * mm, "end": v(2.45, 0.65) * mm});
            skLineSegment(sketch, "E16.1.0.50", {"start": v(2.25, 2.55) * mm, "end": v(2.85, 2.55) * mm});
            skArc(sketch, "E16.1.0.51", {"start": v(3.05, 3.35) * mm, "mid": v(3.2, 3.2) * mm, "end": v(3.05, 3.05) * mm});
            skLineSegment(sketch, "E16.1.0.52", {"start": v(0.5, 0.55) * mm, "end": v(0.7, 0.55) * mm});
            skArc(sketch, "E16.1.0.53", {"start": v(4, 0.74) * mm, "mid": v(3.94, 0.8) * mm, "end": v(4, 0.85) * mm});
            skLineSegment(sketch, "E16.1.0.54", {"start": v(4, 0.74) * mm, "end": v(4.2, 0.74) * mm});
            skLineSegment(sketch, "E16.1.0.55", {"start": v(2.25, 1.45) * mm, "end": v(2.65, 1.45) * mm});
            skLineSegment(sketch, "E16.1.0.56", {"start": v(4, 1.65) * mm, "end": v(4.4, 1.65) * mm});
            skLineSegment(sketch, "E16.1.0.57", {"start": v(2.25, 0.8) * mm, "end": v(2.45, 0.8) * mm, "construction": true});
            skLineSegment(sketch, "E16.1.0.58", {"start": v(0.5, 1.85) * mm, "end": v(0.9, 1.85) * mm});
            skLineSegment(sketch, "E16.1.0.59", {"start": v(0.5, 0.8) * mm, "end": v(0.5, -4) * mm, "construction": true});
            skLineSegment(sketch, "E16.1.0.60", {"start": v(4, 1.54) * mm, "end": v(4.4, 1.54) * mm});
            skLineSegment(sketch, "E16.1.0.61", {"start": v(2.25, 0.95) * mm, "end": v(2.45, 0.95) * mm});
            skLineSegment(sketch, "E16.1.0.62", {"start": v(4, 0.85) * mm, "end": v(4.2, 0.85) * mm});
            skLineSegment(sketch, "E16.1.0.63", {"start": v(2.25, 0.65) * mm, "end": v(2.45, 0.65) * mm});
            skLineSegment(sketch, "E16.1.0.64", {"start": v(0.5, 1.6) * mm, "end": v(0.9, 1.6) * mm, "construction": true});
            skLineSegment(sketch, "E16.1.0.65", {"start": v(2.25, 1.75) * mm, "end": v(2.65, 1.75) * mm});
            skLineSegment(sketch, "E16.1.0.66", {"start": v(4, 1.6) * mm, "end": v(4.4, 1.6) * mm, "construction": true});
            skLineSegment(sketch, "E16.1.0.67", {"start": v(4, 0.8) * mm, "end": v(4.2, 0.8) * mm, "construction": true});
            skLineSegment(sketch, "E16.1.0.68", {"start": v(0.5, 1.05) * mm, "end": v(0.7, 1.05) * mm});
            skArc(sketch, "E16.1.0.69", {"start": v(2.25, 3.05) * mm, "mid": v(2.1, 3.2) * mm, "end": v(2.25, 3.35) * mm});
            skArc(sketch, "E16.1.0.70", {"start": v(4, 1.54) * mm, "mid": v(3.94, 1.6) * mm, "end": v(4, 1.65) * mm});
            skLineSegment(sketch, "E16.1.0.71", {"start": v(0.5, 1.35) * mm, "end": v(0.9, 1.35) * mm});
            skArc(sketch, "E16.1.0.72", {"start": v(4, 3.14) * mm, "mid": v(3.94, 3.2) * mm, "end": v(4, 3.25) * mm});
            skArc(sketch, "E16.1.0.73", {"start": v(4, 2.34) * mm, "mid": v(3.94, 2.4) * mm, "end": v(4, 2.45) * mm});
            skLineSegment(sketch, "E16.1.0.74", {"start": v(2.25, 1.6) * mm, "end": v(2.65, 1.6) * mm, "construction": true});
            skArc(sketch, "E16.1.0.75", {"start": v(4, 3.94) * mm, "mid": v(3.94, 4) * mm, "end": v(4, 4.05) * mm});
            skLineSegment(sketch, "E16.1.0.76", {"start": v(0.5, 0.8) * mm, "end": v(0.7, 0.8) * mm, "construction": true});
            skLineSegment(sketch, "E16.1.1.0", {"start": v(4, -1.54) * mm, "end": v(4.8, -1.54) * mm});
            skArc(sketch, "E16.1.1.1", {"start": v(0.9, -2.95) * mm, "mid": v(1.15, -3.2) * mm, "end": v(0.9, -3.45) * mm});
            skLineSegment(sketch, "E16.1.1.2", {"start": v(0.5, -2.65) * mm, "end": v(1.1, -2.65) * mm});
            skArc(sketch, "E16.1.1.3", {"start": v(0.5, -1.05) * mm, "mid": v(0.25, -0.8) * mm, "end": v(0.5, -0.55) * mm});
            skArc(sketch, "E16.1.1.4", {"start": v(4.2, -3.95) * mm, "mid": v(4.25, -4) * mm, "end": v(4.2, -4.06) * mm});
            skArc(sketch, "E16.1.1.5", {"start": v(4.8, -1.55) * mm, "mid": v(4.85, -1.6) * mm, "end": v(4.8, -1.66) * mm});
            skArc(sketch, "E16.1.1.6", {"start": v(2.65, -3.05) * mm, "mid": v(2.8, -3.2) * mm, "end": v(2.65, -3.35) * mm});
            skLineSegment(sketch, "E16.1.1.7", {"start": v(4, -1.65) * mm, "end": v(4.8, -1.65) * mm});
            skLineSegment(sketch, "E16.1.1.8", {"start": v(0.5, -1.6) * mm, "end": v(1.3, -1.6) * mm, "construction": true});
            skLineSegment(sketch, "E16.1.1.9", {"start": v(0.5, -1.85) * mm, "end": v(1.3, -1.85) * mm});
            skArc(sketch, "E16.1.1.10", {"start": v(1.1, -2.15) * mm, "mid": v(1.35, -2.4) * mm, "end": v(1.1, -2.65) * mm});
            skArc(sketch, "E16.1.1.11", {"start": v(2.25, -4.15) * mm, "mid": v(2.1, -4) * mm, "end": v(2.25, -3.85) * mm});
            skLineSegment(sketch, "E16.1.1.12", {"start": v(4, -0.74) * mm, "end": v(5, -0.74) * mm});
            skArc(sketch, "E16.1.1.13", {"start": v(2.85, -2.25) * mm, "mid": v(3, -2.4) * mm, "end": v(2.85, -2.55) * mm});
            skArc(sketch, "E16.1.1.14", {"start": v(0.5, -4.25) * mm, "mid": v(0.25, -4) * mm, "end": v(0.5, -3.75) * mm});
            skLineSegment(sketch, "E16.1.1.15", {"start": v(4, -0.85) * mm, "end": v(5, -0.85) * mm});
            skLineSegment(sketch, "E16.1.1.16", {"start": v(0.5, -0.8) * mm, "end": v(1.5, -0.8) * mm, "construction": true});
            skLineSegment(sketch, "E16.1.1.17", {"start": v(4, -2.45) * mm, "end": v(4.6, -2.45) * mm});
            skLineSegment(sketch, "E16.1.1.18", {"start": v(2.25, -0.95) * mm, "end": v(3.25, -0.95) * mm});
            skArc(sketch, "E16.1.1.19", {"start": v(4.6, -2.35) * mm, "mid": v(4.65, -2.4) * mm, "end": v(4.6, -2.46) * mm});
            skLineSegment(sketch, "E16.1.1.20", {"start": v(0.5, -1.05) * mm, "end": v(1.5, -1.05) * mm});
            skArc(sketch, "E16.1.1.21", {"start": v(3.25, -0.65) * mm, "mid": v(3.4, -0.8) * mm, "end": v(3.25, -0.95) * mm});
            skLineSegment(sketch, "E16.1.1.22", {"start": v(2.25, -2.55) * mm, "end": v(2.85, -2.55) * mm});
            skLineSegment(sketch, "E16.1.1.23", {"start": v(4, -2.4) * mm, "end": v(4.6, -2.4) * mm, "construction": true});
            skLineSegment(sketch, "E16.1.1.24", {"start": v(0.5, -2.4) * mm, "end": v(1.1, -2.4) * mm, "construction": true});
            skArc(sketch, "E16.1.1.25", {"start": v(2.25, -2.55) * mm, "mid": v(2.1, -2.4) * mm, "end": v(2.25, -2.25) * mm});
            skLineSegment(sketch, "E16.1.1.26", {"start": v(4, -0.8) * mm, "end": v(5, -0.8) * mm, "construction": true});
            skLineSegment(sketch, "E16.1.1.27", {"start": v(2.25, -0.8) * mm, "end": v(3.25, -0.8) * mm, "construction": true});
            skArc(sketch, "E16.1.1.28", {"start": v(5, -0.75) * mm, "mid": v(5.05, -0.8) * mm, "end": v(5, -0.86) * mm});
            skArc(sketch, "E16.1.1.29", {"start": v(1.3, -1.35) * mm, "mid": v(1.55, -1.6) * mm, "end": v(1.3, -1.85) * mm});
            skLineSegment(sketch, "E16.1.1.30", {"start": v(0.5, -4) * mm, "end": v(2.25, -4) * mm, "construction": true});
            skLineSegment(sketch, "E16.1.1.31", {"start": v(2.25, -1.75) * mm, "end": v(3.05, -1.75) * mm});
            skArc(sketch, "E16.1.1.32", {"start": v(0.5, -1.85) * mm, "mid": v(0.25, -1.6) * mm, "end": v(0.5, -1.35) * mm});
            skLineSegment(sketch, "E16.1.1.33", {"start": v(4, -1.6) * mm, "end": v(4.8, -1.6) * mm, "construction": true});
            skLineSegment(sketch, "E16.1.1.34", {"start": v(2.25, -2.4) * mm, "end": v(2.85, -2.4) * mm, "construction": true});
            skLineSegment(sketch, "E16.1.1.35", {"start": v(0.5, -1.35) * mm, "end": v(1.3, -1.35) * mm});
            skLineSegment(sketch, "E16.1.1.36", {"start": v(2.25, -1.45) * mm, "end": v(3.05, -1.45) * mm});
            skLineSegment(sketch, "E16.1.1.37", {"start": v(2.25, -0.65) * mm, "end": v(3.25, -0.65) * mm});
            skArc(sketch, "E16.1.1.38", {"start": v(2.25, -0.95) * mm, "mid": v(2.1, -0.8) * mm, "end": v(2.25, -0.65) * mm});
            skArc(sketch, "E16.1.1.39", {"start": v(0.5, -3.45) * mm, "mid": v(0.25, -3.2) * mm, "end": v(0.5, -2.95) * mm});
            skArc(sketch, "E16.1.1.40", {"start": v(1.5, -0.55) * mm, "mid": v(1.75, -0.8) * mm, "end": v(1.5, -1.05) * mm});
            skArc(sketch, "E16.1.1.41", {"start": v(2.25, -3.35) * mm, "mid": v(2.1, -3.2) * mm, "end": v(2.25, -3.05) * mm});
            skLineSegment(sketch, "E16.1.1.42", {"start": v(0.5, -2.15) * mm, "end": v(1.1, -2.15) * mm});
            skArc(sketch, "E16.1.1.43", {"start": v(0.7, -3.75) * mm, "mid": v(0.95, -4) * mm, "end": v(0.7, -4.25) * mm});
            skLineSegment(sketch, "E16.1.1.44", {"start": v(4, -2.34) * mm, "end": v(4.6, -2.34) * mm});
            skLineSegment(sketch, "E16.1.1.45", {"start": v(2.25, -1.6) * mm, "end": v(3.05, -1.6) * mm, "construction": true});
            skArc(sketch, "E16.1.1.46", {"start": v(0.5, -2.65) * mm, "mid": v(0.25, -2.4) * mm, "end": v(0.5, -2.15) * mm});
            skLineSegment(sketch, "E16.1.1.47", {"start": v(0.5, -0.55) * mm, "end": v(1.5, -0.55) * mm});
            skArc(sketch, "E16.1.1.48", {"start": v(4.4, -3.15) * mm, "mid": v(4.45, -3.2) * mm, "end": v(4.4, -3.26) * mm});
            skArc(sketch, "E16.1.1.49", {"start": v(2.45, -3.85) * mm, "mid": v(2.6, -4) * mm, "end": v(2.45, -4.15) * mm});
            skLineSegment(sketch, "E16.1.1.50", {"start": v(2.25, -2.25) * mm, "end": v(2.85, -2.25) * mm});
            skArc(sketch, "E16.1.1.51", {"start": v(3.05, -1.45) * mm, "mid": v(3.2, -1.6) * mm, "end": v(3.05, -1.75) * mm});
            skLineSegment(sketch, "E16.1.1.52", {"start": v(0.5, -4.25) * mm, "end": v(0.7, -4.25) * mm});
            skArc(sketch, "E16.1.1.53", {"start": v(4, -4.06) * mm, "mid": v(3.94, -4) * mm, "end": v(4, -3.94) * mm});
            skLineSegment(sketch, "E16.1.1.54", {"start": v(4, -4.05) * mm, "end": v(4.2, -4.05) * mm});
            skLineSegment(sketch, "E16.1.1.55", {"start": v(2.25, -3.35) * mm, "end": v(2.65, -3.35) * mm});
            skLineSegment(sketch, "E16.1.1.56", {"start": v(4, -3.14) * mm, "end": v(4.4, -3.14) * mm});
            skLineSegment(sketch, "E16.1.1.57", {"start": v(2.25, -4) * mm, "end": v(2.45, -4) * mm, "construction": true});
            skLineSegment(sketch, "E16.1.1.58", {"start": v(0.5, -2.95) * mm, "end": v(0.9, -2.95) * mm});
            skLineSegment(sketch, "E16.1.1.59", {"start": v(0.5, -4) * mm, "end": v(0.5, -8.8) * mm, "construction": true});
            skLineSegment(sketch, "E16.1.1.60", {"start": v(4, -3.25) * mm, "end": v(4.4, -3.25) * mm});
            skLineSegment(sketch, "E16.1.1.61", {"start": v(2.25, -3.85) * mm, "end": v(2.45, -3.85) * mm});
            skLineSegment(sketch, "E16.1.1.62", {"start": v(4, -3.94) * mm, "end": v(4.2, -3.94) * mm});
            skLineSegment(sketch, "E16.1.1.63", {"start": v(2.25, -4.15) * mm, "end": v(2.45, -4.15) * mm});
            skLineSegment(sketch, "E16.1.1.64", {"start": v(0.5, -3.2) * mm, "end": v(0.9, -3.2) * mm, "construction": true});
            skLineSegment(sketch, "E16.1.1.65", {"start": v(2.25, -3.05) * mm, "end": v(2.65, -3.05) * mm});
            skLineSegment(sketch, "E16.1.1.66", {"start": v(4, -3.2) * mm, "end": v(4.4, -3.2) * mm, "construction": true});
            skLineSegment(sketch, "E16.1.1.67", {"start": v(4, -4) * mm, "end": v(4.2, -4) * mm, "construction": true});
            skLineSegment(sketch, "E16.1.1.68", {"start": v(0.5, -3.75) * mm, "end": v(0.7, -3.75) * mm});
            skArc(sketch, "E16.1.1.69", {"start": v(2.25, -1.75) * mm, "mid": v(2.1, -1.6) * mm, "end": v(2.25, -1.45) * mm});
            skArc(sketch, "E16.1.1.70", {"start": v(4, -3.26) * mm, "mid": v(3.94, -3.2) * mm, "end": v(4, -3.15) * mm});
            skLineSegment(sketch, "E16.1.1.71", {"start": v(0.5, -3.45) * mm, "end": v(0.9, -3.45) * mm});
            skArc(sketch, "E16.1.1.72", {"start": v(4, -1.66) * mm, "mid": v(3.94, -1.6) * mm, "end": v(4, -1.55) * mm});
            skArc(sketch, "E16.1.1.73", {"start": v(4, -2.46) * mm, "mid": v(3.94, -2.4) * mm, "end": v(4, -2.35) * mm});
            skLineSegment(sketch, "E16.1.1.74", {"start": v(2.25, -3.2) * mm, "end": v(2.65, -3.2) * mm, "construction": true});
            skArc(sketch, "E16.1.1.75", {"start": v(4, -0.86) * mm, "mid": v(3.94, -0.8) * mm, "end": v(4, -0.75) * mm});
            skLineSegment(sketch, "E16.1.1.76", {"start": v(0.5, -4) * mm, "end": v(0.7, -4) * mm, "construction": true});
            skLineSegment(sketch, "E16.direction1", {"start": v(-4.75, -4) * mm, "end": v(0.5, -4) * mm, "construction": true});
            skLineSegment(sketch, "E16.direction2", {"start": v(-4.75, -4) * mm, "end": v(-4.75, -8.8) * mm, "construction": true});
            skSolve(sketch);
        }
        {
            var Q0;
            Q0 = qSketchRegion(id + "F2", true);
            var Q1;
            Q1=makeQuery(id+"F2.imprint","IMPRINT",FACE,{"disambiguationData":[TD([[makeQuery(id+"F2.imprint","IMPRINT",EDGE,{"derivedFrom":sQuery(id+"F2.wireOp",EDGE,"E13.4.startCap")}),-1.0]])]});
            var Q2;
            Q2=makeQuery(id+"F2.imprint","IMPRINT",FACE,{"disambiguationData":[TD([[makeQuery(id+"F2.imprint","IMPRINT",EDGE,{"derivedFrom":sQuery(id+"F2.wireOp",EDGE,"E13.3.startCap")}),-1.0]])]});
            var Q3;
            Q3=makeQuery(id+"F2.imprint","IMPRINT",FACE,{"disambiguationData":[TD([[makeQuery(id+"F2.imprint","IMPRINT",EDGE,{"derivedFrom":sQuery(id+"F2.wireOp",EDGE,"E13.2.startCap")}),-1.0]])]});
            var Q4;
            Q4=makeQuery(id+"F2.imprint","IMPRINT",FACE,{"disambiguationData":[TD([[makeQuery(id+"F2.imprint","IMPRINT",EDGE,{"derivedFrom":sQuery(id+"F2.wireOp",EDGE,"E13.1.startCap")}),-1.0]])]});
            var Q5;
            Q5=makeQuery(id+"F2.imprint","IMPRINT",FACE,{"disambiguationData":[TD([[makeQuery(id+"F2.imprint","IMPRINT",EDGE,{"derivedFrom":sQuery(id+"F2.wireOp",EDGE,"E13.0.startCap")}),-1.0]])]});
            var Q6;
            Q6=makeQuery(id+"F2.imprint","IMPRINT",FACE,{"disambiguationData":[TD([[makeQuery(id+"F2.imprint","IMPRINT",EDGE,{"derivedFrom":sQuery(id+"F2.wireOp",EDGE,"E14.4.startCap")}),-1.0]])]});
            var Q7;
            Q7=makeQuery(id+"F2.imprint","IMPRINT",FACE,{"disambiguationData":[TD([[makeQuery(id+"F2.imprint","IMPRINT",EDGE,{"derivedFrom":sQuery(id+"F2.wireOp",EDGE,"E14.3.startCap")}),-1.0]])]});
            var Q8;
            Q8=makeQuery(id+"F2.imprint","IMPRINT",FACE,{"disambiguationData":[TD([[makeQuery(id+"F2.imprint","IMPRINT",EDGE,{"derivedFrom":sQuery(id+"F2.wireOp",EDGE,"E14.2.startCap")}),-1.0]])]});
            var Q9;
            Q9=makeQuery(id+"F2.imprint","IMPRINT",FACE,{"disambiguationData":[TD([[makeQuery(id+"F2.imprint","IMPRINT",EDGE,{"derivedFrom":sQuery(id+"F2.wireOp",EDGE,"E14.1.startCap")}),-1.0]])]});
            var Q10;
            Q10=makeQuery(id+"F2.imprint","IMPRINT",FACE,{"disambiguationData":[TD([[makeQuery(id+"F2.imprint","IMPRINT",EDGE,{"derivedFrom":sQuery(id+"F2.wireOp",EDGE,"E14.0.startCap")}),-1.0]])]});
            var Q11;
            Q11=makeQuery(id+"F2.imprint","IMPRINT",FACE,{"disambiguationData":[TD([[makeQuery(id+"F2.imprint","IMPRINT",EDGE,{"derivedFrom":sQuery(id+"F2.wireOp",EDGE,"E15.0.startCap")}),-1.0]])]});
            var Q12;
            Q12=makeQuery(id+"F2.imprint","IMPRINT",FACE,{"disambiguationData":[TD([[makeQuery(id+"F2.imprint","IMPRINT",EDGE,{"derivedFrom":sQuery(id+"F2.wireOp",EDGE,"E15.1.startCap")}),-1.0]])]});
            var Q13;
            Q13=makeQuery(id+"F2.imprint","IMPRINT",FACE,{"disambiguationData":[TD([[makeQuery(id+"F2.imprint","IMPRINT",EDGE,{"derivedFrom":sQuery(id+"F2.wireOp",EDGE,"E15.2.startCap")}),-1.0]])]});
            var Q14;
            Q14=makeQuery(id+"F2.imprint","IMPRINT",FACE,{"disambiguationData":[TD([[makeQuery(id+"F2.imprint","IMPRINT",EDGE,{"derivedFrom":sQuery(id+"F2.wireOp",EDGE,"E15.3.startCap")}),-1.0]])]});
            var Q15;
            Q15=makeQuery(id+"F2.imprint","IMPRINT",FACE,{"disambiguationData":[TD([[makeQuery(id+"F2.imprint","IMPRINT",EDGE,{"derivedFrom":sQuery(id+"F2.wireOp",EDGE,"E15.4.startCap")}),-1.0]])]});
            extrude(context, id + "F3", {"entities" : qUnion([Q0, Q1, Q2, Q3, Q4, Q5, Q6, Q7, Q8, Q9, Q10, Q11, Q12, Q13, Q14, Q15]), "operationType" : NewBodyOperationType.REMOVE, "oppositeDirection" : true, "depth" : 0.4 * mm, "offsetDistance" : 25 * mm});
        }
        {
            var Q0;
            Q0=makeQuery(id+"F2.imprint","IMPRINT",FACE,{"disambiguationData":[TD([[makeQuery(id+"F2.imprint","IMPRINT",EDGE,{"derivedFrom":sQuery(id+"F2.wireOp",EDGE,"E16.1.0.3")}),-1.0]])]});
            var Q1;
            Q1=makeQuery(id+"F2.imprint","IMPRINT",FACE,{"disambiguationData":[TD([[makeQuery(id+"F2.imprint","IMPRINT",EDGE,{"derivedFrom":sQuery(id+"F2.wireOp",EDGE,"E16.1.0.18")}),1.0]])]});
            var Q2;
            Q2=makeQuery(id+"F2.imprint","IMPRINT",FACE,{"disambiguationData":[TD([[makeQuery(id+"F2.imprint","IMPRINT",EDGE,{"derivedFrom":sQuery(id+"F2.wireOp",EDGE,"E16.1.0.12")}),-1.0]])]});
            var Q3;
            Q3=makeQuery(id+"F2.imprint","IMPRINT",FACE,{"disambiguationData":[TD([[makeQuery(id+"F2.imprint","IMPRINT",EDGE,{"derivedFrom":sQuery(id+"F2.wireOp",EDGE,"E16.1.0.0")}),-1.0]])]});
            var Q4;
            Q4=makeQuery(id+"F2.imprint","IMPRINT",FACE,{"disambiguationData":[TD([[makeQuery(id+"F2.imprint","IMPRINT",EDGE,{"derivedFrom":sQuery(id+"F2.wireOp",EDGE,"E16.1.0.31")}),1.0]])]});
            var Q5;
            Q5=makeQuery(id+"F2.imprint","IMPRINT",FACE,{"disambiguationData":[TD([[makeQuery(id+"F2.imprint","IMPRINT",EDGE,{"derivedFrom":sQuery(id+"F2.wireOp",EDGE,"E16.1.0.9")}),1.0]])]});
            var Q6;
            Q6=makeQuery(id+"F2.imprint","IMPRINT",FACE,{"disambiguationData":[TD([[makeQuery(id+"F2.imprint","IMPRINT",EDGE,{"derivedFrom":sQuery(id+"F2.wireOp",EDGE,"E16.1.0.2")}),1.0]])]});
            var Q7;
            Q7=makeQuery(id+"F2.imprint","IMPRINT",FACE,{"disambiguationData":[TD([[makeQuery(id+"F2.imprint","IMPRINT",EDGE,{"derivedFrom":sQuery(id+"F2.wireOp",EDGE,"E16.1.0.13")}),-1.0]])]});
            var Q8;
            Q8=makeQuery(id+"F2.imprint","IMPRINT",FACE,{"disambiguationData":[TD([[makeQuery(id+"F2.imprint","IMPRINT",EDGE,{"derivedFrom":sQuery(id+"F2.wireOp",EDGE,"E16.1.0.17")}),1.0]])]});
            var Q9;
            Q9=makeQuery(id+"F2.imprint","IMPRINT",FACE,{"disambiguationData":[TD([[makeQuery(id+"F2.imprint","IMPRINT",EDGE,{"derivedFrom":sQuery(id+"F2.wireOp",EDGE,"E16.1.0.48")}),-1.0]])]});
            var Q10;
            Q10=makeQuery(id+"F2.imprint","IMPRINT",FACE,{"disambiguationData":[TD([[makeQuery(id+"F2.imprint","IMPRINT",EDGE,{"derivedFrom":sQuery(id+"F2.wireOp",EDGE,"E16.1.0.6")}),-1.0]])]});
            var Q11;
            Q11=makeQuery(id+"F2.imprint","IMPRINT",FACE,{"disambiguationData":[TD([[makeQuery(id+"F2.imprint","IMPRINT",EDGE,{"derivedFrom":sQuery(id+"F2.wireOp",EDGE,"E16.1.0.1")}),-1.0]])]});
            var Q12;
            Q12=makeQuery(id+"F2.imprint","IMPRINT",FACE,{"disambiguationData":[TD([[makeQuery(id+"F2.imprint","IMPRINT",EDGE,{"derivedFrom":sQuery(id+"F2.wireOp",EDGE,"E16.1.0.14")}),-1.0]])]});
            var Q13;
            Q13=makeQuery(id+"F2.imprint","IMPRINT",FACE,{"disambiguationData":[TD([[makeQuery(id+"F2.imprint","IMPRINT",EDGE,{"derivedFrom":sQuery(id+"F2.wireOp",EDGE,"E16.1.0.11")}),-1.0]])]});
            var Q14;
            Q14=makeQuery(id+"F2.imprint","IMPRINT",FACE,{"disambiguationData":[TD([[makeQuery(id+"F2.imprint","IMPRINT",EDGE,{"derivedFrom":sQuery(id+"F2.wireOp",EDGE,"E16.1.0.4")}),-1.0]])]});
            extrude(context, id + "F4", {"entities" : qUnion([Q0, Q1, Q2, Q3, Q4, Q5, Q6, Q7, Q8, Q9, Q10, Q11, Q12, Q13, Q14]), "operationType" : NewBodyOperationType.REMOVE, "oppositeDirection" : true, "depth" : .3 * mm, "offsetDistance" : 25 * mm});
        }
        {
            var Q0;
            Q0=makeQuery(id+"F2.imprint","IMPRINT",FACE,{"disambiguationData":[TD([[makeQuery(id+"F2.imprint","IMPRINT",EDGE,{"derivedFrom":sQuery(id+"F2.wireOp",EDGE,"E16.0.1.3")}),-1.0]])]});
            var Q1;
            Q1=makeQuery(id+"F2.imprint","IMPRINT",FACE,{"disambiguationData":[TD([[makeQuery(id+"F2.imprint","IMPRINT",EDGE,{"derivedFrom":sQuery(id+"F2.wireOp",EDGE,"E16.0.1.18")}),1.0]])]});
            var Q2;
            Q2=makeQuery(id+"F2.imprint","IMPRINT",FACE,{"disambiguationData":[TD([[makeQuery(id+"F2.imprint","IMPRINT",EDGE,{"derivedFrom":sQuery(id+"F2.wireOp",EDGE,"E16.0.1.12")}),-1.0]])]});
            var Q3;
            Q3=makeQuery(id+"F2.imprint","IMPRINT",FACE,{"disambiguationData":[TD([[makeQuery(id+"F2.imprint","IMPRINT",EDGE,{"derivedFrom":sQuery(id+"F2.wireOp",EDGE,"E16.0.1.9")}),1.0]])]});
            var Q4;
            Q4=makeQuery(id+"F2.imprint","IMPRINT",FACE,{"disambiguationData":[TD([[makeQuery(id+"F2.imprint","IMPRINT",EDGE,{"derivedFrom":sQuery(id+"F2.wireOp",EDGE,"E16.0.1.31")}),1.0]])]});
            var Q5;
            Q5=makeQuery(id+"F2.imprint","IMPRINT",FACE,{"disambiguationData":[TD([[makeQuery(id+"F2.imprint","IMPRINT",EDGE,{"derivedFrom":sQuery(id+"F2.wireOp",EDGE,"E16.0.1.0")}),-1.0]])]});
            var Q6;
            Q6=makeQuery(id+"F2.imprint","IMPRINT",FACE,{"disambiguationData":[TD([[makeQuery(id+"F2.imprint","IMPRINT",EDGE,{"derivedFrom":sQuery(id+"F2.wireOp",EDGE,"E16.0.1.2")}),1.0]])]});
            var Q7;
            Q7=makeQuery(id+"F2.imprint","IMPRINT",FACE,{"disambiguationData":[TD([[makeQuery(id+"F2.imprint","IMPRINT",EDGE,{"derivedFrom":sQuery(id+"F2.wireOp",EDGE,"E16.0.1.13")}),-1.0]])]});
            var Q8;
            Q8=makeQuery(id+"F2.imprint","IMPRINT",FACE,{"disambiguationData":[TD([[makeQuery(id+"F2.imprint","IMPRINT",EDGE,{"derivedFrom":sQuery(id+"F2.wireOp",EDGE,"E16.0.1.17")}),1.0]])]});
            var Q9;
            Q9=makeQuery(id+"F2.imprint","IMPRINT",FACE,{"disambiguationData":[TD([[makeQuery(id+"F2.imprint","IMPRINT",EDGE,{"derivedFrom":sQuery(id+"F2.wireOp",EDGE,"E16.0.1.1")}),-1.0]])]});
            var Q10;
            Q10=makeQuery(id+"F2.imprint","IMPRINT",FACE,{"disambiguationData":[TD([[makeQuery(id+"F2.imprint","IMPRINT",EDGE,{"derivedFrom":sQuery(id+"F2.wireOp",EDGE,"E16.0.1.6")}),-1.0]])]});
            var Q11;
            Q11=makeQuery(id+"F2.imprint","IMPRINT",FACE,{"disambiguationData":[TD([[makeQuery(id+"F2.imprint","IMPRINT",EDGE,{"derivedFrom":sQuery(id+"F2.wireOp",EDGE,"E16.0.1.48")}),-1.0]])]});
            var Q12;
            Q12=makeQuery(id+"F2.imprint","IMPRINT",FACE,{"disambiguationData":[TD([[makeQuery(id+"F2.imprint","IMPRINT",EDGE,{"derivedFrom":sQuery(id+"F2.wireOp",EDGE,"E16.0.1.14")}),-1.0]])]});
            var Q13;
            Q13=makeQuery(id+"F2.imprint","IMPRINT",FACE,{"disambiguationData":[TD([[makeQuery(id+"F2.imprint","IMPRINT",EDGE,{"derivedFrom":sQuery(id+"F2.wireOp",EDGE,"E16.0.1.11")}),-1.0]])]});
            var Q14;
            Q14=makeQuery(id+"F2.imprint","IMPRINT",FACE,{"disambiguationData":[TD([[makeQuery(id+"F2.imprint","IMPRINT",EDGE,{"derivedFrom":sQuery(id+"F2.wireOp",EDGE,"E16.0.1.4")}),-1.0]])]});
            extrude(context, id + "F5", {"entities" : qUnion([Q0, Q1, Q2, Q3, Q4, Q5, Q6, Q7, Q8, Q9, Q10, Q11, Q12, Q13, Q14]), "operationType" : NewBodyOperationType.REMOVE, "oppositeDirection" : true, "depth" : .2 * mm, "offsetDistance" : 25 * mm});
        }
        {
            var Q0;
            Q0=makeQuery(id+"F2.imprint","IMPRINT",FACE,{"disambiguationData":[TD([[makeQuery(id+"F2.imprint","IMPRINT",EDGE,{"derivedFrom":sQuery(id+"F2.wireOp",EDGE,"E16.1.1.3")}),-1.0]])]});
            var Q1;
            Q1=makeQuery(id+"F2.imprint","IMPRINT",FACE,{"disambiguationData":[TD([[makeQuery(id+"F2.imprint","IMPRINT",EDGE,{"derivedFrom":sQuery(id+"F2.wireOp",EDGE,"E16.1.1.18")}),1.0]])]});
            var Q2;
            Q2=makeQuery(id+"F2.imprint","IMPRINT",FACE,{"disambiguationData":[TD([[makeQuery(id+"F2.imprint","IMPRINT",EDGE,{"derivedFrom":sQuery(id+"F2.wireOp",EDGE,"E16.1.1.12")}),-1.0]])]});
            var Q3;
            Q3=makeQuery(id+"F2.imprint","IMPRINT",FACE,{"disambiguationData":[TD([[makeQuery(id+"F2.imprint","IMPRINT",EDGE,{"derivedFrom":sQuery(id+"F2.wireOp",EDGE,"E16.1.1.9")}),1.0]])]});
            var Q4;
            Q4=makeQuery(id+"F2.imprint","IMPRINT",FACE,{"disambiguationData":[TD([[makeQuery(id+"F2.imprint","IMPRINT",EDGE,{"derivedFrom":sQuery(id+"F2.wireOp",EDGE,"E16.1.1.31")}),1.0]])]});
            var Q5;
            Q5=makeQuery(id+"F2.imprint","IMPRINT",FACE,{"disambiguationData":[TD([[makeQuery(id+"F2.imprint","IMPRINT",EDGE,{"derivedFrom":sQuery(id+"F2.wireOp",EDGE,"E16.1.1.0")}),-1.0]])]});
            var Q6;
            Q6=makeQuery(id+"F2.imprint","IMPRINT",FACE,{"disambiguationData":[TD([[makeQuery(id+"F2.imprint","IMPRINT",EDGE,{"derivedFrom":sQuery(id+"F2.wireOp",EDGE,"E16.1.1.2")}),1.0]])]});
            var Q7;
            Q7=makeQuery(id+"F2.imprint","IMPRINT",FACE,{"disambiguationData":[TD([[makeQuery(id+"F2.imprint","IMPRINT",EDGE,{"derivedFrom":sQuery(id+"F2.wireOp",EDGE,"E16.1.1.13")}),-1.0]])]});
            var Q8;
            Q8=makeQuery(id+"F2.imprint","IMPRINT",FACE,{"disambiguationData":[TD([[makeQuery(id+"F2.imprint","IMPRINT",EDGE,{"derivedFrom":sQuery(id+"F2.wireOp",EDGE,"E16.1.1.17")}),1.0]])]});
            var Q9;
            Q9=makeQuery(id+"F2.imprint","IMPRINT",FACE,{"disambiguationData":[TD([[makeQuery(id+"F2.imprint","IMPRINT",EDGE,{"derivedFrom":sQuery(id+"F2.wireOp",EDGE,"E16.1.1.1")}),-1.0]])]});
            var Q10;
            Q10=makeQuery(id+"F2.imprint","IMPRINT",FACE,{"disambiguationData":[TD([[makeQuery(id+"F2.imprint","IMPRINT",EDGE,{"derivedFrom":sQuery(id+"F2.wireOp",EDGE,"E16.1.1.6")}),-1.0]])]});
            var Q11;
            Q11=makeQuery(id+"F2.imprint","IMPRINT",FACE,{"disambiguationData":[TD([[makeQuery(id+"F2.imprint","IMPRINT",EDGE,{"derivedFrom":sQuery(id+"F2.wireOp",EDGE,"E16.1.1.48")}),-1.0]])]});
            var Q12;
            Q12=makeQuery(id+"F2.imprint","IMPRINT",FACE,{"disambiguationData":[TD([[makeQuery(id+"F2.imprint","IMPRINT",EDGE,{"derivedFrom":sQuery(id+"F2.wireOp",EDGE,"E16.1.1.14")}),-1.0]])]});
            var Q13;
            Q13=makeQuery(id+"F2.imprint","IMPRINT",FACE,{"disambiguationData":[TD([[makeQuery(id+"F2.imprint","IMPRINT",EDGE,{"derivedFrom":sQuery(id+"F2.wireOp",EDGE,"E16.1.1.11")}),-1.0]])]});
            var Q14;
            Q14=makeQuery(id+"F2.imprint","IMPRINT",FACE,{"disambiguationData":[TD([[makeQuery(id+"F2.imprint","IMPRINT",EDGE,{"derivedFrom":sQuery(id+"F2.wireOp",EDGE,"E16.1.1.4")}),-1.0]])]});
            extrude(context, id + "F6", {"entities" : qUnion([Q0, Q1, Q2, Q3, Q4, Q5, Q6, Q7, Q8, Q9, Q10, Q11, Q12, Q13, Q14]), "operationType" : NewBodyOperationType.REMOVE, "oppositeDirection" : true, "depth" : .1 * mm, "offsetDistance" : 25 * mm});
        }
        {
            var Q0;
            Q0=makeQuery(id+"F2.imprint","IMPRINT",FACE,{"disambiguationData":[TD([[makeQuery(id+"F2.imprint","IMPRINT",EDGE,{"derivedFrom":sQuery(id+"F2.wireOp",EDGE,"E8.0")}),-1.0]])]});
            extrude(context, id + "F7", {"entities" : qUnion([Q0]), "operationType" : NewBodyOperationType.ADD, "depth" : .5 * mm, "offsetDistance" : 25 * mm});
        }
    });
